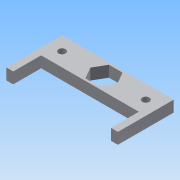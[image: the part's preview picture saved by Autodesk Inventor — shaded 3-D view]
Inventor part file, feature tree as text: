
AUTODESK INVENTOR PART (.ipt)
format: ipt  version: 2015 (Build 190159000, 159)  size: 140,288 bytes
history: native  units: mm
features: extrude x4, sketch x3, reference x2, projected_geometry x1
ambient origin geometry x8: Origin, YZ Plane, XZ Plane, XY Plane, X Axis, Y Axis, Z Axis, Center Point
bodies: Solid1 (feature_tree)
feature tree (10):
  extrude  "Extrusion1"  Depth=20.0mm
  extrude  "Extrusion2"  Depth=10.0mm TaperAngle=0.0deg
  extrude  "Extrusion3"  Depth=8.0mm
  extrude  "Extrusion7"  Depth=10.0mm TaperAngle=0.0deg
  sketch  "Sketch3"  dims[d0=80.0mm d1=20.0mm]
  sketch  "Sketch9"  dims[d2=8.0mm d3=0.0mm d13=10.0mm d14=0.0mm]
  reference  "Reference1"
  reference  "Reference2"
  sketch  "Sketch14"  dims[d40=5.2mm d41=60.0mm d42=10.0mm d43=0.0mm d65=19.5mm d70=40.0mm d73=10.0mm d74=5.0mm d75=20.0mm d76=8.0mm d77=0.0mm]
  projected_geometry  "Projected Loop2"
